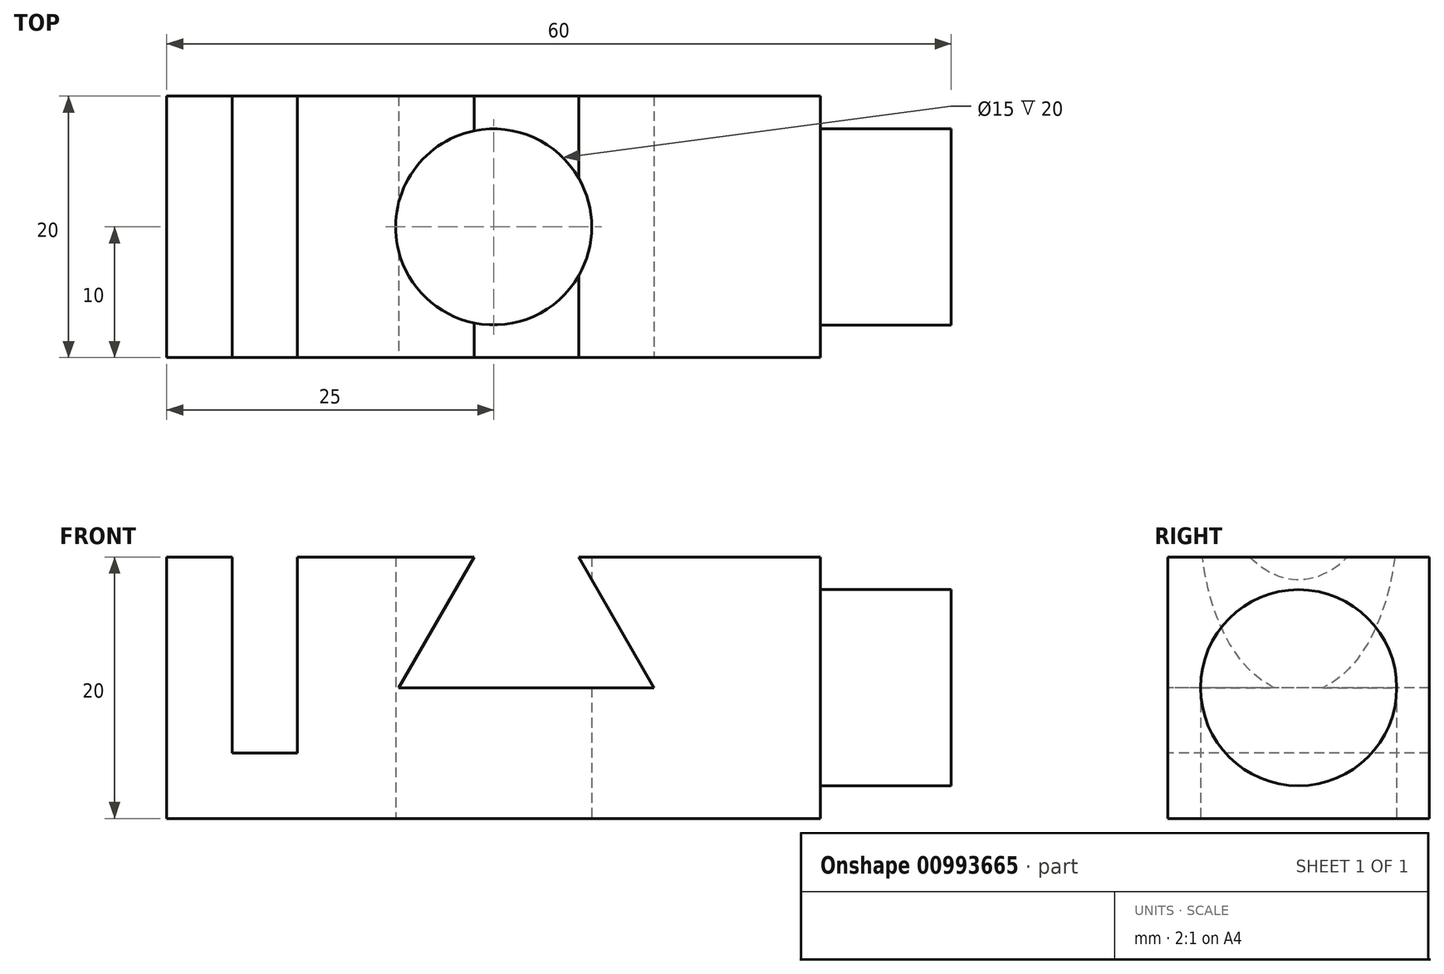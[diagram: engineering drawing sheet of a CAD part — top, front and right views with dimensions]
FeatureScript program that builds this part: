
annotation { "Feature Type Name" : "Feature", "Feature Type Description" : "" }
export const myFeature = defineFeature(function(context is Context, id is Id, definition is map)
    precondition{}
    {
        {
            var Q0;
            Q0=qCreatedBy(makeId("Top.planeOp"),FACE);
            var sketch = newSketch(context, id + "F0", { "sketchPlane" : qUnion([Q0])});
            skLineSegment(sketch, "E0.bottom", {"start": v(25, -10) * mm, "end": v(-25, -10) * mm});
            skLineSegment(sketch, "E0.top", {"start": v(25, 10) * mm, "end": v(-25, 10) * mm});
            skLineSegment(sketch, "E0.left", {"start": v(25, -10) * mm, "end": v(25, 10) * mm});
            skLineSegment(sketch, "E0.right", {"start": v(-25, -10) * mm, "end": v(-25, 10) * mm});
            skPoint(sketch, "E0.middle", {"position": v(0, 0) * mm});
            skCircle(sketch, "E1", {"center": v(0, 0) * mm, "radius": 7.5 * mm});
            skSolve(sketch);
        }
        {
            var Q0;
            Q0=makeQuery(id+"F0.imprint","IMPRINT",FACE,{"disambiguationData":[TD([[makeQuery(id+"F0.imprint","IMPRINT",EDGE,{"derivedFrom":sQuery(id+"F0.wireOp",EDGE,"E0.bottom")}),-1.0]])]});
            extrude(context, id + "F1", {"entities" : qUnion([Q0]), "depth" : 20 * mm, "offsetDistance" : 25.4 * mm});
        }
        {
            var Q0;
            Q0=makeQuery(id+"F1.opExtrude","CAP_FACE",FACE,{"disambiguationData":[OSD([sQuery(id+"F0.wireOp",EDGE,"E0.bottom"),sQuery(id+"F0.wireOp",EDGE,"E0.top"),sQuery(id+"F0.wireOp",EDGE,"E0.left"),sQuery(id+"F0.wireOp",EDGE,"E0.right"),sQuery(id+"F0.wireOp",EDGE,"E1")])],"isStart":false});
            var sketch = newSketch(context, id + "F2", { "sketchPlane" : qUnion([Q0])});
            skLineSegment(sketch, "E2.bottom", {"start": v(-20, 10) * mm, "end": v(-15, 10) * mm});
            skLineSegment(sketch, "E2.top", {"start": v(-20, -10) * mm, "end": v(-15, -10) * mm});
            skLineSegment(sketch, "E2.left", {"start": v(-20, 10) * mm, "end": v(-20, -10) * mm});
            skLineSegment(sketch, "E2.right", {"start": v(-15, 10) * mm, "end": v(-15, -10) * mm});
            skSolve(sketch);
        }
        {
            var Q0;
            Q0=makeQuery(id+"F2.imprint","IMPRINT",FACE,{"disambiguationData":[TD([[makeQuery(id+"F2.imprint","IMPRINT",EDGE,{"derivedFrom":sQuery(id+"F2.wireOp",EDGE,"E2.bottom")}),1.0]])]});
            extrude(context, id + "F3", {"entities" : qUnion([Q0]), "operationType" : NewBodyOperationType.REMOVE, "oppositeDirection" : true, "depth" : 15 * mm, "offsetDistance" : 25 * mm});
        }
        {
            var Q0;
            Q0=makeQuery(id+"F1.opExtrude","SWEPT_FACE",FACE,{"disambiguationData":[OSD([sQuery(id+"F0.wireOp",EDGE,"E0.bottom")])]});
            var sketch = newSketch(context, id + "F4", { "sketchPlane" : qUnion([Q0])});
            skLineSegment(sketch, "E3", {"start": v(-1.5, 20) * mm, "end": v(-7.27, 10) * mm});
            skLineSegment(sketch, "E4", {"start": v(12.27, 10) * mm, "end": v(6.5, 20) * mm});
            skLineSegment(sketch, "E5", {"start": v(6.5, 20) * mm, "end": v(-1.5, 20) * mm});
            skLineSegment(sketch, "E6", {"start": v(-7.27, 10) * mm, "end": v(12.27, 10) * mm});
            skLineSegment(sketch, "E7", {"start": v(2.5, 10) * mm, "end": v(2.5, 20) * mm, "construction": true});
            skSolve(sketch);
        }
        {
            var Q0;
            Q0=makeQuery(id+"F4.imprint","IMPRINT",FACE,{"disambiguationData":[TD([[makeQuery(id+"F4.imprint","IMPRINT",EDGE,{"derivedFrom":sQuery(id+"F4.wireOp",EDGE,"E3")}),1.0]])]});
            extrude(context, id + "F5", {"entities" : qUnion([Q0]), "operationType" : NewBodyOperationType.REMOVE, "endBound" : BoundingType.THROUGH_ALL, "oppositeDirection" : true, "depth" : 10 * mm, "offsetDistance" : 25 * mm});
        }
        {
            var Q0;
            Q0=makeQuery(id+"F1.opExtrude","SWEPT_FACE",FACE,{"disambiguationData":[OSD([sQuery(id+"F0.wireOp",EDGE,"E0.left")])]});
            var sketch = newSketch(context, id + "F6", { "sketchPlane" : qUnion([Q0])});
            skCircle(sketch, "E8", {"center": v(0, 10) * mm, "radius": 7.5 * mm});
            skPoint(sketch, "E8.centerSnap0", {"position": v(-10, 10) * mm});
            skPoint(sketch, "E8.centerSnap1", {"position": v(0, 20) * mm});
            skSolve(sketch);
        }
        {
            var Q0;
            Q0=makeQuery(id+"F6.imprint","IMPRINT",FACE,{"disambiguationData":[TD([[makeQuery(id+"F6.imprint","IMPRINT",EDGE,{"derivedFrom":sQuery(id+"F6.wireOp",EDGE,"E8")}),1.0]])]});
            extrude(context, id + "F7", {"entities" : qUnion([Q0]), "operationType" : NewBodyOperationType.ADD, "depth" : 10 * mm, "offsetDistance" : 25 * mm});
        }
    });
